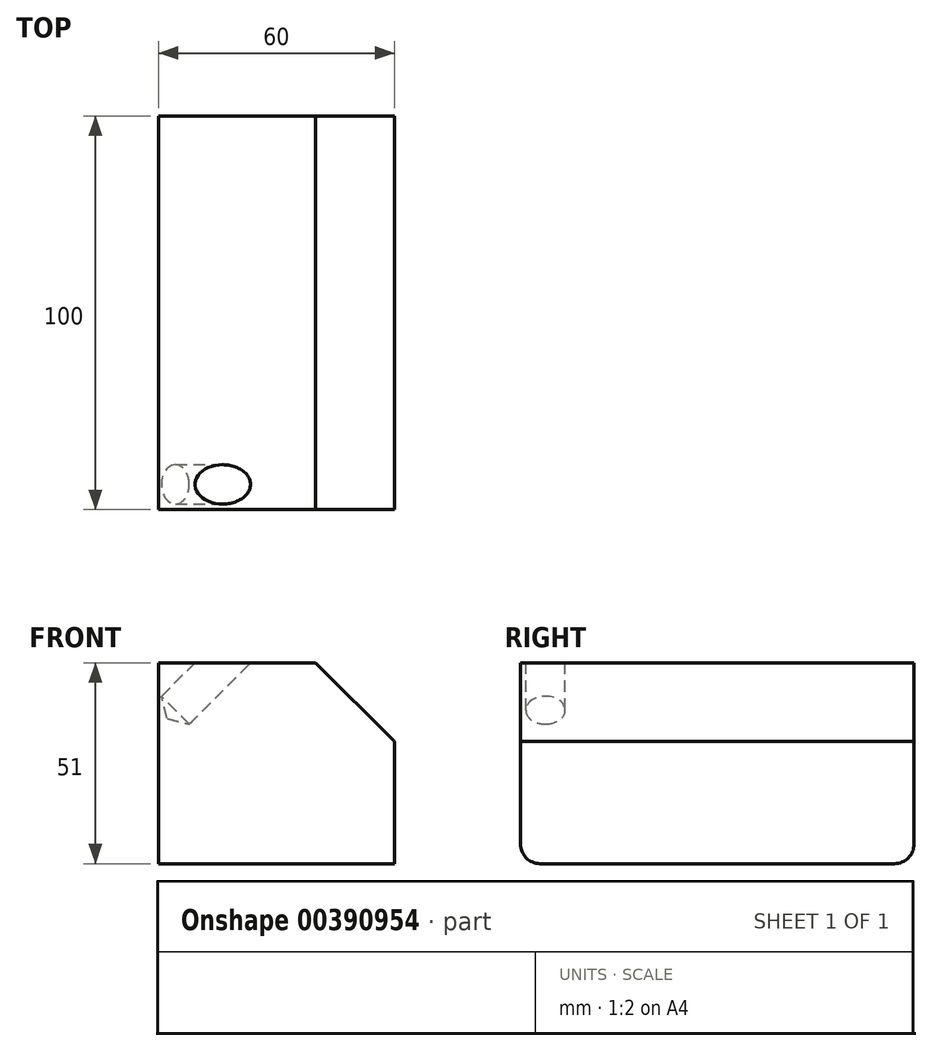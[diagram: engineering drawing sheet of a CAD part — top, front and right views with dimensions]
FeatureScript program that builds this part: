
annotation { "Feature Type Name" : "Feature", "Feature Type Description" : "" }
export const myFeature = defineFeature(function(context is Context, id is Id, definition is map)
    precondition{}
    {
        {
            var Q0;
            Q0=qCreatedBy(makeId("Top.planeOp"),FACE);
            var sketch = newSketch(context, id + "F0", { "sketchPlane" : qUnion([Q0])});
            skLineSegment(sketch, "E0.bottom", {"start": v(0, 0) * mm, "end": v(60, 0) * mm});
            skLineSegment(sketch, "E0.top", {"start": v(0, 100) * mm, "end": v(60, 100) * mm});
            skLineSegment(sketch, "E0.left", {"start": v(0, 0) * mm, "end": v(0, 100) * mm});
            skLineSegment(sketch, "E0.right", {"start": v(60, 0) * mm, "end": v(60, 100) * mm});
            skSolve(sketch);
        }
        {
            var Q0;
            Q0 = qSketchRegion(id + "F0", true);
            extrude(context, id + "F1", {"entities" : qUnion([Q0]), "depth" : 51 * mm});
        }
        {
            var Q0;
            Q0=makeQuery(id+"F1.opExtrude","CAP_EDGE",EDGE,{"disambiguationData":[OSD([sQuery(id+"F0.wireOp",EDGE,"E0.right")])],"isStart":false});
            chamfer(context, id + "F2", {"entities" : qUnion([Q0]), "width" : 20 * mm, "tangentPropagation" : true});
        }
        {
            var Q0;
            Q0=makeQuery(id+"F2.opChamfer","BLEND_FACE",FACE,{"disambiguationData":[OSD([sQuery(id+"F0.wireOp",EDGE,"E0.right")])]});
            var sketch = newSketch(context, id + "F3", { "sketchPlane" : qUnion([Q0])});
            skPoint(sketch, "E1", {"position": v(6.36, 24.5) * mm});
            skPoint(sketch, "E1.positionSnap0", {"position": v(6.36, 0) * mm});
            skPoint(sketch, "E2", {"position": v(6.36, 68) * mm});
            skSolve(sketch);
        }
        {
            var Q0;
            Q0=sQuery(id+"F3.wireOp",VERTEX,"E1");
            var Q1;
            Q1=sQuery(id+"F3.wireOp",VERTEX,"E2");
            var Q2;
            Q2=makeQuery(id+"F1.opExtrude","SWEPT_BODY",BODY,{"disambiguationData":[OSD([sQuery(id+"F0.wireOp",EDGE,"E0.bottom"),sQuery(id+"F0.wireOp",EDGE,"E0.top"),sQuery(id+"F0.wireOp",EDGE,"E0.left"),sQuery(id+"F0.wireOp",EDGE,"E0.right")])]});
            hole(context, id + "F4", {"style" : HoleStyle.SIMPLE, "endStyle" : HoleEndStyle.BLIND, "standardTappedOrClearance" : lookupTablePath({ "standard" : "ISO", "size" : "10", "type" : "Drilled" }), "standardBlindInLast" : lookupTablePath({ "standard" : "ISO", "size" : "10", "type" : "Drilled" }), "holeDiameter" : 10 * mm, "holeDepth" : 12 * mm, "isTappedThrough" : true, "tappedDepth" : 12 * mm, "tapClearance" : 3, "locations" : qUnion([Q0, Q1]), "scope" : qUnion([Q2])});
        }
        {
            var Q0;
            Q0=makeQuery(id+"F1.opExtrude","CAP_EDGE",EDGE,{"disambiguationData":[OSD([sQuery(id+"F0.wireOp",EDGE,"E0.top")])],"isStart":true});
            var Q1;
            Q1=makeQuery(id+"F1.opExtrude","CAP_EDGE",EDGE,{"disambiguationData":[OSD([sQuery(id+"F0.wireOp",EDGE,"E0.bottom")])],"isStart":true});
            fillet(context, id + "F5", {"entities" : qUnion([Q0, Q1]), "radius" : 5 * mm, "tangentPropagation" : true, "allowEdgeOverflow" : false});
        }
    });
